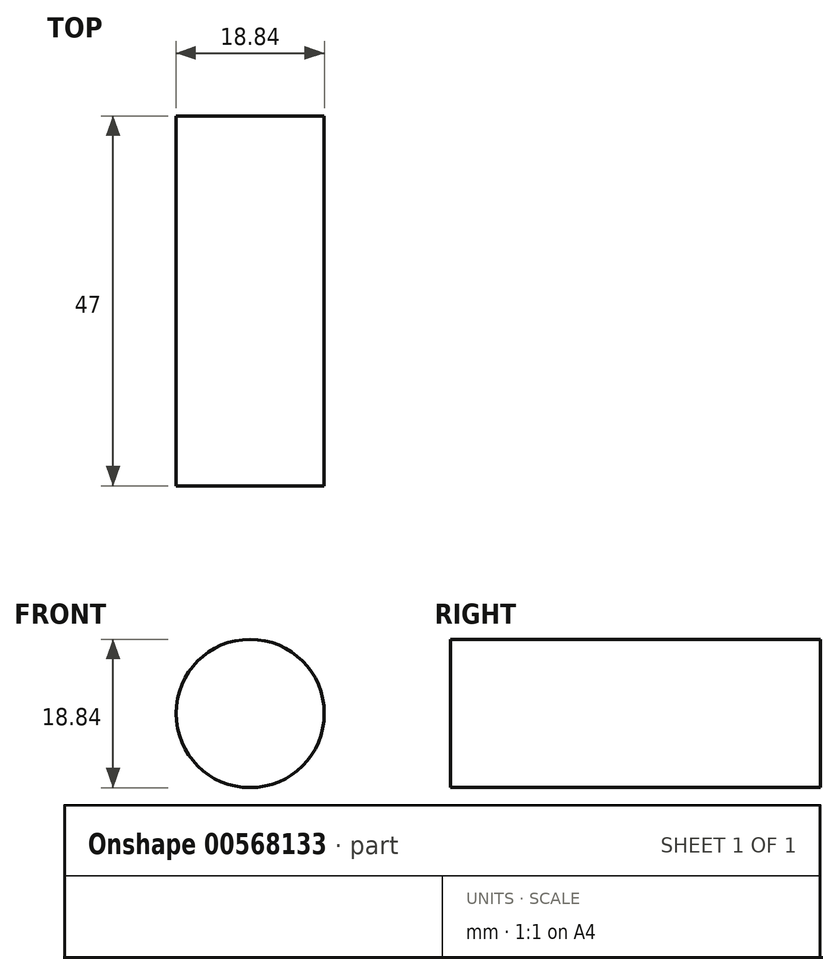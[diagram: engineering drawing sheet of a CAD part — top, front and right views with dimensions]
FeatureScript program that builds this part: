
annotation { "Feature Type Name" : "Feature", "Feature Type Description" : "" }
export const myFeature = defineFeature(function(context is Context, id is Id, definition is map)
    precondition{}
    {
        {
            var Q0;
            Q0=qCreatedBy(makeId("Front.planeOp"),FACE);
            var sketch = newSketch(context, id + "F0", { "sketchPlane" : qUnion([Q0])});
            skCircle(sketch, "E0", {"center": v(0, 0) * mm, "radius": 9.42 * mm});
            skSolve(sketch);
        }
        {
            var Q0;
            Q0=makeQuery(id+"F0.imprint","IMPRINT",FACE,{"disambiguationData":[TD([[makeQuery(id+"F0.imprint","IMPRINT",EDGE,{"derivedFrom":sQuery(id+"F0.wireOp",EDGE,"E0")}),1.0]])]});
            extrude(context, id + "F1", {"entities" : qUnion([Q0]), "endBound" : BoundingType.SYMMETRIC, "depth" : 47 * mm, "offsetDistance" : 25.4 * mm});
        }
    });
